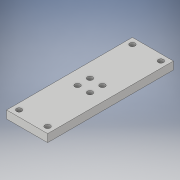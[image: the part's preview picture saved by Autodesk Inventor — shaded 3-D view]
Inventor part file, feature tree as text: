
AUTODESK INVENTOR PART (.ipt)
format: ipt  version: 2019.4 (Build 234330000, 330)  size: 124,928 bytes
history: native  units: in
note: dims shown in document units (in); Inventor stores cm internally (conversion verified against a paired STEP export)
features: sketch x3, hole x2, extrude x1
ambient origin geometry x8: Origin, YZ Plane, XZ Plane, XY Plane, X Axis, Y Axis, Z Axis, Center Point
bodies: Solid1 (feature_tree)
feature tree (6):
  extrude  "Extrusion1"  Depth=1.0354in
  hole  "Hole1"  [1 undecoded]
  hole  "Hole2"  [1 undecoded]
  sketch  "Sketch1"  dims[d0=3.1772in d1=1.0354in]
  sketch  "Sketch2"  dims[d2=0.1969in d3=0.0in d4=0.1181in]
  sketch  "Sketch3"  dims[d5=0.1575in d6=0.1575in d7=0.1575in d8=0.1575in d9=0.1339in d10=0.339in d11=0.248in d12=0.25in d13=90.0deg d14=0.617in d15=0.8108in d16=0.1181in d17=0.1575in d18=0.1575in d19=0.1575in d20=0.1575in d21=0.1339in d22=0.339in d23=0.119in d24=0.25in d25=0.5635in d26=0.617in d27=0.8108in]
note: 2 required parameter values undecoded (feature->parameter linkage not recoverable at this tier; creation-order binding heuristic only, values carry confidence <= 0.55)
